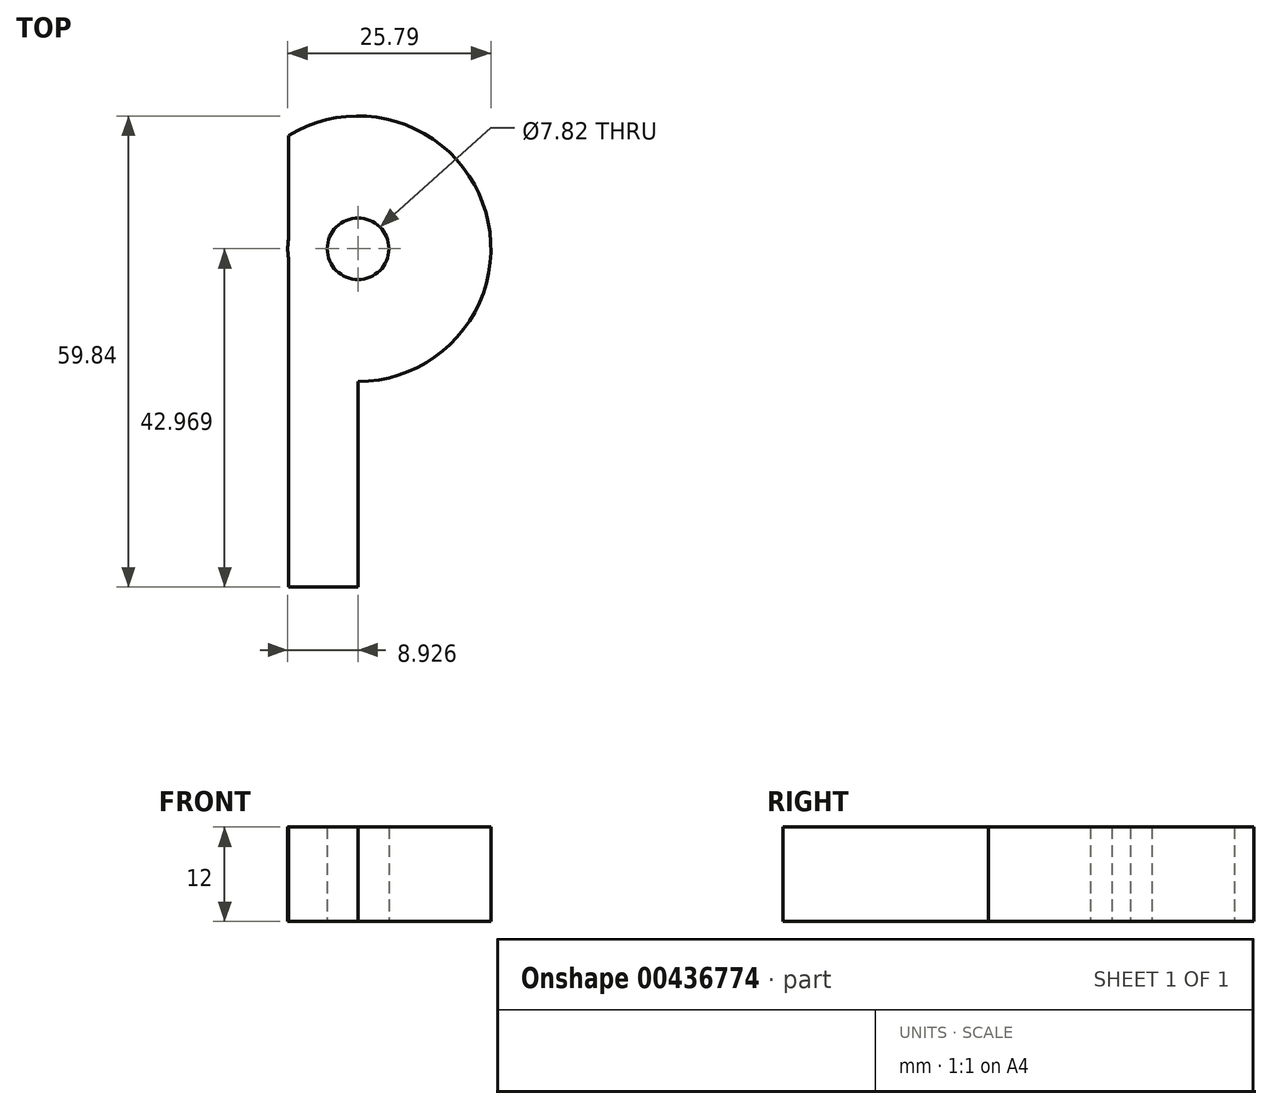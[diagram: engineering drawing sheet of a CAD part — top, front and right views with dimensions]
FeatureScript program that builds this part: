
annotation { "Feature Type Name" : "Feature", "Feature Type Description" : "" }
export const myFeature = defineFeature(function(context is Context, id is Id, definition is map)
    precondition{}
    {
        {
            var Q0;
            Q0=qCreatedBy(makeId("Top.planeOp"),FACE);
            var sketch = newSketch(context, id + "F0", { "sketchPlane" : qUnion([Q0])});
            skLineSegment(sketch, "E0", {"start": v(0, 0) * mm, "end": v(0, 27.77) * mm});
            skLineSegment(sketch, "E1", {"start": v(0, 0) * mm, "end": v(0, -32.07) * mm});
            skLineSegment(sketch, "E2", {"start": v(0, -32.07) * mm, "end": v(8.86, -32.07) * mm});
            skLineSegment(sketch, "E3", {"start": v(8.86, -32.07) * mm, "end": v(8.86, -5.97) * mm});
            skLineSegment(sketch, "E4", {"start": v(0, 27.77) * mm, "end": v(0, 2.63) * mm});
            skLineSegment(sketch, "E5", {"start": v(8.86, 0) * mm, "end": v(8.86, 1.97) * mm});
            skPoint(sketch, "E6.end.orphan", {"position": v(29.92, 0) * mm});
            skArc(sketch, "E7", {"start": v(0, -3.46) * mm, "mid": v(25.72, 10.9) * mm, "end": v(0, 25.25) * mm});
            skArc(sketch, "E8", {"start": v(0, 12.05) * mm, "mid": v(-0.07, 10.9) * mm, "end": v(0, 9.75) * mm});
            skArc(sketch, "E9", {"start": v(0, 4.34) * mm, "mid": v(19.88, 10.9) * mm, "end": v(0, 17.45) * mm});
            skPoint(sketch, "E10.start.orphan", {"position": v(2.15, 27.77) * mm});
            skCircle(sketch, "E11", {"center": v(8.86, 10.9) * mm, "radius": 3.91 * mm});
            skSolve(sketch);
        }
        {
            var Q0;
            Q0 = qSketchRegion(id + "F0", true);
            extrude(context, id + "F1", {"entities" : qUnion([Q0]), "depth" : 12 * mm});
        }
    });
